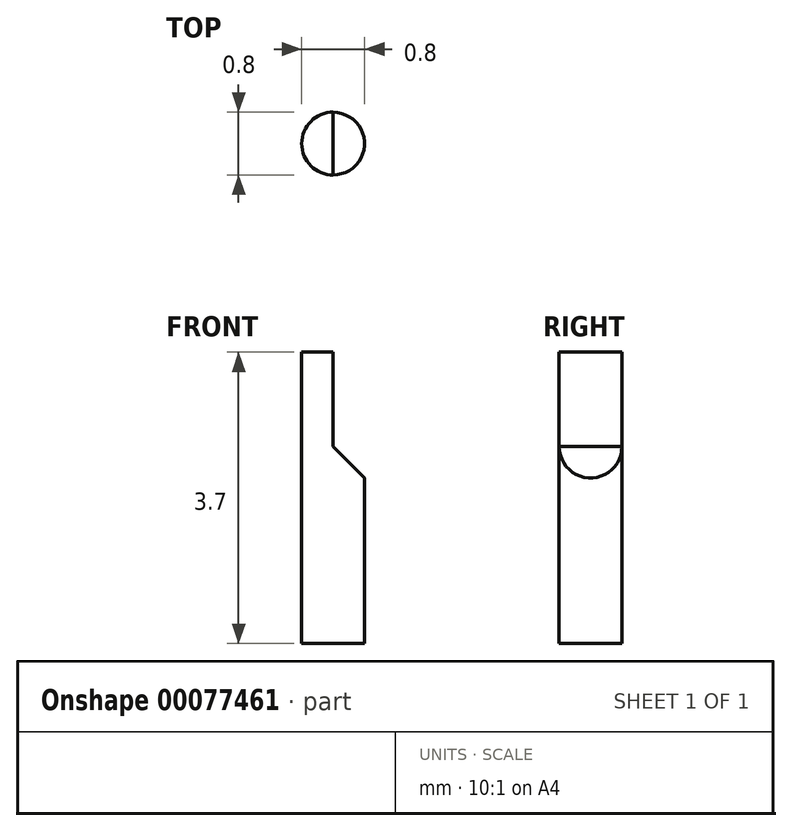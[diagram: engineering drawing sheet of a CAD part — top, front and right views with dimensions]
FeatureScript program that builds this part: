
annotation { "Feature Type Name" : "Feature", "Feature Type Description" : "" }
export const myFeature = defineFeature(function(context is Context, id is Id, definition is map)
    precondition{}
    {
        {
            var Q0;
            Q0=qCreatedBy(makeId("Top.planeOp"),FACE);
            var sketch = newSketch(context, id + "F0", { "sketchPlane" : qUnion([Q0])});
            skCircle(sketch, "E0", {"center": v(0, 0) * mm, "radius": 0.4 * mm});
            skSolve(sketch);
        }
        {
            var Q0;
            Q0=makeQuery(id+"F0.imprint","IMPRINT",FACE,{"disambiguationData":[TD([[makeQuery(id+"F0.imprint","IMPRINT",EDGE,{"derivedFrom":sQuery(id+"F0.wireOp",EDGE,"E0")}),1.0]])]});
            extrude(context, id + "F1", {"entities" : qUnion([Q0]), "depth" : 3.7 * mm});
        }
        {
            var Q0;
            Q0=makeQuery(id+"F1.opExtrude","SWEPT_BODY",BODY,{"disambiguationData":[OSD([sQuery(id+"F0.wireOp",EDGE,"E0")])]});
            transform(context, id + "F2", {"entities" : qUnion([Q0]), "transformType" : TransformType.TRANSLATION_3D, "dx" : 0 * mm, "dy" : 0 * mm, "dz" : 0 * mm, "makeCopy" : true});
        }
        {
            var Q0;
            Q0=qCreatedBy(makeId("Front.planeOp"),FACE);
            var sketch = newSketch(context, id + "F3", { "sketchPlane" : qUnion([Q0])});
            skLineSegment(sketch, "E1", {"start": v(0, 0) * mm, "end": v(0, 3.7) * mm, "construction": true});
            skLineSegment(sketch, "E2", {"start": v(0, 3.7) * mm, "end": v(0, 2.5) * mm});
            skLineSegment(sketch, "E3", {"start": v(0, 2.5) * mm, "end": v(0.4, 2.1) * mm});
            skLineSegment(sketch, "E4", {"start": v(0.4, 2.1) * mm, "end": v(0.4, 3.7) * mm});
            skLineSegment(sketch, "E5", {"start": v(0.4, 3.7) * mm, "end": v(0, 3.7) * mm});
            skSolve(sketch);
        }
        {
            var Q0;
            Q0=makeQuery(id+"F3.imprint","IMPRINT",FACE,{"disambiguationData":[TD([[makeQuery(id+"F3.imprint","IMPRINT",EDGE,{"derivedFrom":sQuery(id+"F3.wireOp",EDGE,"E2")}),1.0]])]});
            extrude(context, id + "F4", {"entities" : qUnion([Q0]), "operationType" : NewBodyOperationType.REMOVE, "oppositeDirection" : true, "depth" : 1 * mm, "symmetric" : true});
        }
    });
